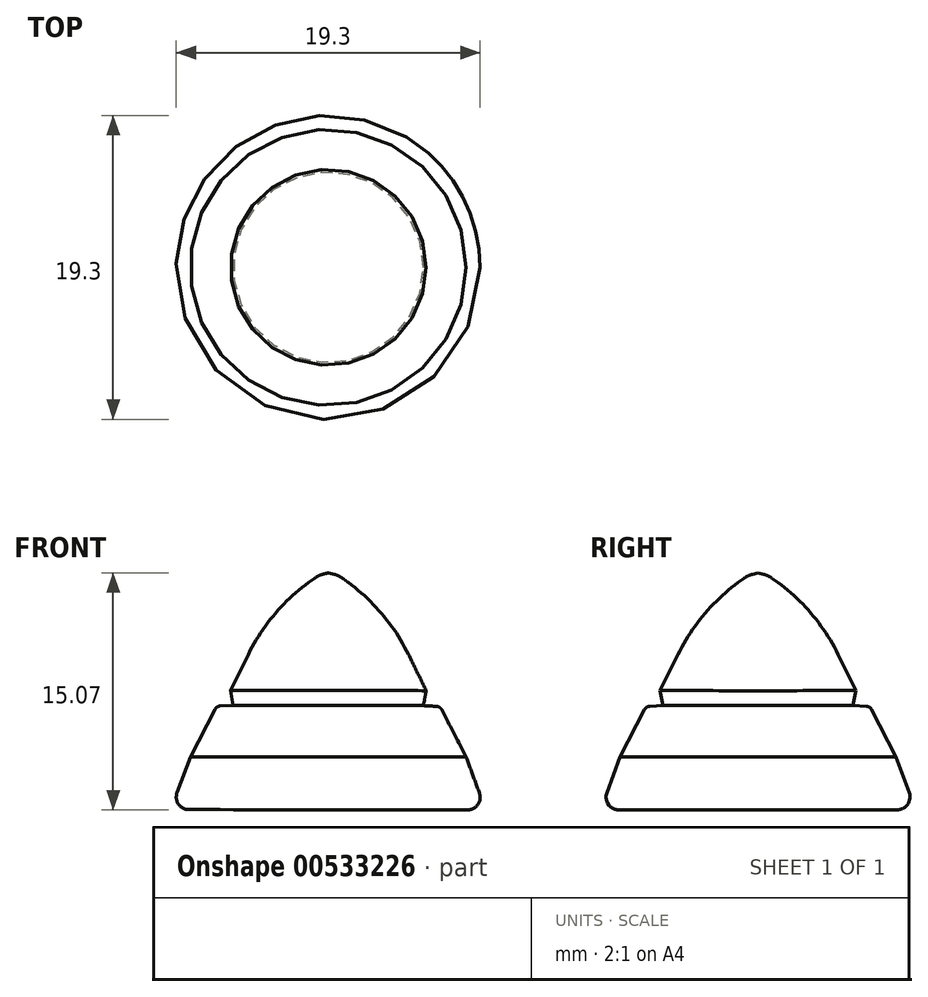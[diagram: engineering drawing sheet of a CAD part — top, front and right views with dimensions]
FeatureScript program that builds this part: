
annotation { "Feature Type Name" : "Feature", "Feature Type Description" : "" }
export const myFeature = defineFeature(function(context is Context, id is Id, definition is map)
    precondition{}
    {
        {
            var Q0;
            Q0=qCreatedBy(makeId("Front.planeOp"),FACE);
            var sketch = newSketch(context, id + "F0", { "sketchPlane" : qUnion([Q0])});
            skLineSegment(sketch, "E0", {"start": v(0, 0) * mm, "end": v(-10, 0) * mm});
            skLineSegment(sketch, "E1", {"start": v(-10, 0) * mm, "end": v(-8.75, 3.36) * mm});
            skLineSegment(sketch, "E2", {"start": v(-8.75, 3.36) * mm, "end": v(-7.1, 6.56) * mm});
            skLineSegment(sketch, "E3", {"start": v(-7.1, 6.56) * mm, "end": v(-6.03, 6.62) * mm});
            skLineSegment(sketch, "E4", {"start": v(-6.03, 6.62) * mm, "end": v(-6.2, 7.57) * mm});
            skLineSegment(sketch, "E5", {"start": v(-6.2, 7.57) * mm, "end": v(-3.71, 12.61) * mm});
            skLineSegment(sketch, "E6", {"start": v(-3.71, 12.61) * mm, "end": v(-0.63, 14.87) * mm});
            skLineSegment(sketch, "E7", {"start": v(-0.63, 14.87) * mm, "end": v(0.02, 15.04) * mm});
            skLineSegment(sketch, "E8", {"start": v(0.02, 15.04) * mm, "end": v(0, 0) * mm});
            skSolve(sketch);
        }
        {
            var Q0;
            Q0=makeQuery(id+"F0.imprint","IMPRINT",FACE,{"disambiguationData":[TD([[makeQuery(id+"F0.imprint","IMPRINT",EDGE,{"derivedFrom":sQuery(id+"F0.wireOp",EDGE,"E0")}),-1.0]])]});
            var Q1;
            Q1=sQuery(id+"F0.wireOp",EDGE,"E8");
            revolve(context, id + "F1", {"entities" : qUnion([Q0]), "axis" : qUnion([Q1]), "revolveType" : RevolveType.FULL});
        }
        {
            var Q0;
            Q0=makeQuery(id+"F1.opRevolve","SWEPT_EDGE",EDGE,{"disambiguationData":[OSD([sQuery(id+"F0.wireOp",EDGE,"E2"),sQuery(id+"F0.wireOp",EDGE,"E3")])]});
            fillet(context, id + "F2", {"entities" : qUnion([Q0]), "radius" : 0.4 * mm, "tangentPropagation" : true, "allowEdgeOverflow" : false});
        }
        {
            var Q0;
            Q0=makeQuery(id+"F1.opRevolve","SWEPT_EDGE",EDGE,{"disambiguationData":[OSD([sQuery(id+"F0.wireOp",EDGE,"E5"),sQuery(id+"F0.wireOp",EDGE,"E6")])]});
            fillet(context, id + "F3", {"entities" : qUnion([Q0]), "radius" : 12.5 * mm, "tangentPropagation" : true, "allowEdgeOverflow" : false});
        }
        {
            var Q0;
            Q0=makeQuery(id+"F1.opRevolve","SWEPT_EDGE",EDGE,{"disambiguationData":[OSD([sQuery(id+"F0.wireOp",EDGE,"E6"),sQuery(id+"F0.wireOp",EDGE,"E7")])]});
            fillet(context, id + "F4", {"entities" : qUnion([Q0]), "radius" : 1.6 * mm, "tangentPropagation" : true, "allowEdgeOverflow" : false});
        }
        {
            var Q0;
            Q0=makeQuery(id+"F1.opRevolve","SWEPT_EDGE",EDGE,{"disambiguationData":[OSD([sQuery(id+"F0.wireOp",EDGE,"E0"),sQuery(id+"F0.wireOp",EDGE,"E1")])]});
            fillet(context, id + "F5", {"entities" : qUnion([Q0]), "radius" : 0.8 * mm, "tangentPropagation" : true, "allowEdgeOverflow" : false});
        }
    });
